# Revit family: QF_Varimixer_ERGO60
name_source: partatom
category: Specialty Equipment
units: mm (PartAtom-declared; Revit-internal decimal feet)

## family parameters
Always vertical = Yes
Cut with Voids When Loaded = No
OmniClass Number = 23.40.40.14.14.11
OmniClass Title = Food Mixers
Part Type = Normal
Room Calculation Point = No
Round Connector Dimension = Use Diameter
Shared = No
Work Plane-Based = No

## types (4) — shared parameters
Bowl size = 60 liter
Depth = 1032 mm  [stored 3.38583 ft]
Description = Planetary mixer ERGO60
Electrical connection height = 1742.4 mm
Height = 1829 mm  [stored 6.00066 ft]
Homepage = https://www.varimixer.com
Ingress protection = IP53 (option IP54)
Length = 1266 mm  [stored 4.15354 ft]
Manufacturer = Varimixer A/S
Model = ERGO60
Panel name = VL-4
Plug included = No
Product description = Planetary mixer, heavy duty for whipping, kneading and mixing. 
Ergonomic - no heavy lifting
Product name = ERGO60
URL = www.varimixer.com
URL datasheet = https://varimixer.com
Weight in Pounds = 686
Weight in kilograms = 330

## per-type parameters (varying)
| type | Connected with neutral | Cycle | Full load current | Horsepower | Number of phases | Power | Voltage |
| 230V/50Hz/3Ph/Europe | Yes | 50 Hz | 8 A |  | 3 | 3000 W | 230 V |
| 400V/50Hz/3Ph/Europe | Yes | 50 Hz | 7 A |  | 3 | 3000 W | 400 V |
| 208V/60Hz/3Ph/USA | Yes | 60 Hz | 13 A | 4 hp | 3 | 3000 W | 208 V |
| Others on Request | No | 0 Hz | 0 A |  | 0 | 0 W | 0 V |

note: [stored X ft] marks values corroborated as IEEE doubles in the binary element streams (Revit-internal decimal feet)

## geometry (parser evidence)
native form markers: Blend x10, Sweep x2
no freeform markers — native parametric forms only
